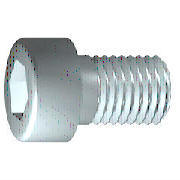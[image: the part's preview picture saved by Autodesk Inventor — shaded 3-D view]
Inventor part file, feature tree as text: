
AUTODESK INVENTOR PART (.ipt)
format: ipt  version: 2022 (Build 260153000, 153)  size: 191,488 bytes
history: native  units: mm (DEFAULTED — no unit token found)
features: sketch x2, other x1, extrude x1, plane x1, fillet x1
ambient origin geometry x7: Origin, YZ Plane, XY Plane, X Axis, Y Axis, Z Axis, Center Point
bodies: Solid1 (feature_tree)
feature tree (6):
  other  "Базовый элемент"
  extrude  "Паз"  Depth=9.0mm
  plane  "Work Plane1"
  fillet  "Fillet2"  Radius=0.24548mm
  sketch  "Эскиз1"
  sketch  "Эскиз2"
